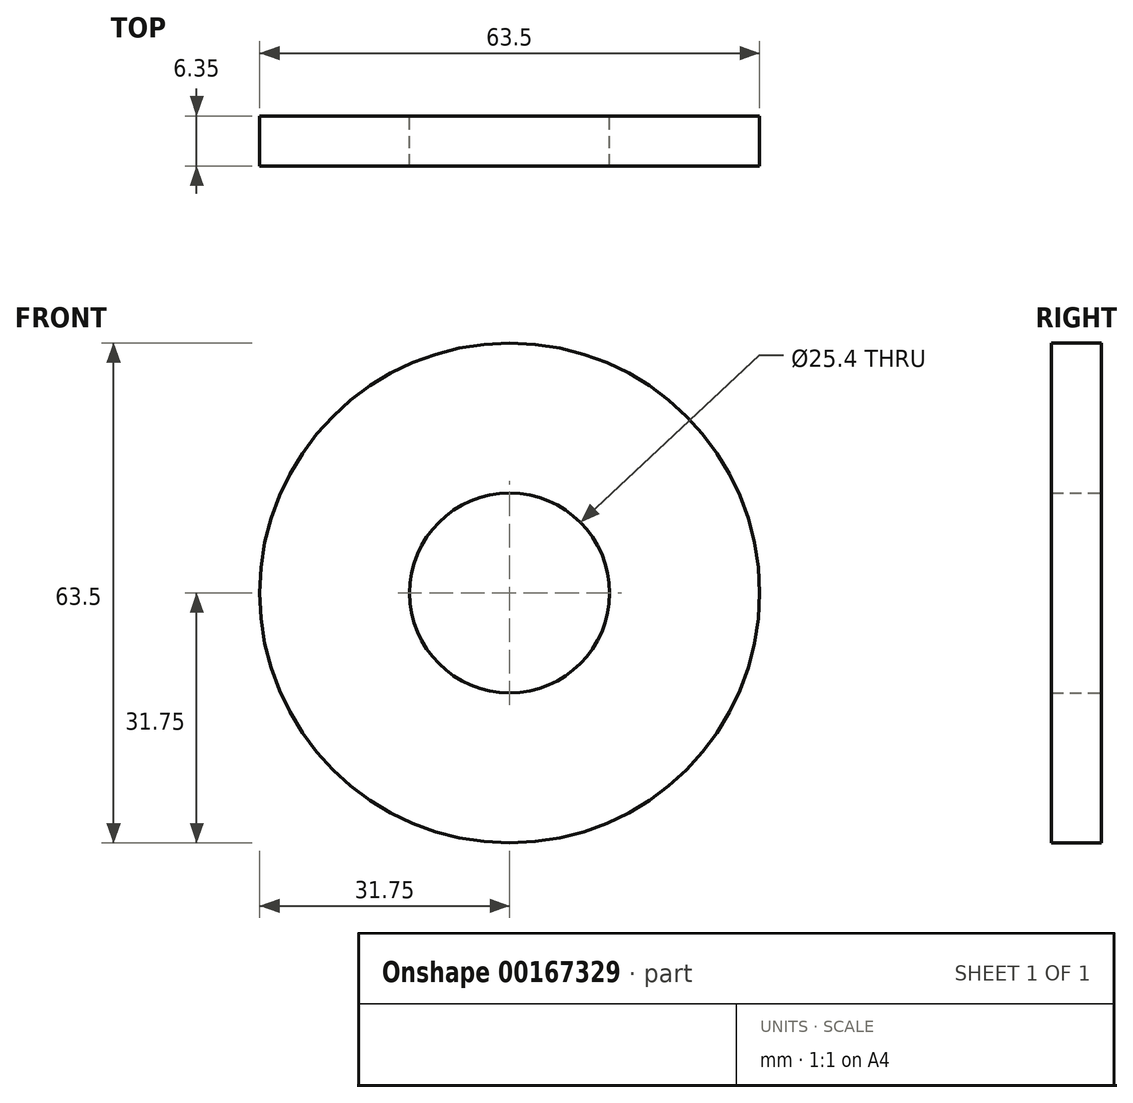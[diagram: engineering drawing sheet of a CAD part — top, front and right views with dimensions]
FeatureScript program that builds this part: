
annotation { "Feature Type Name" : "Feature", "Feature Type Description" : "" }
export const myFeature = defineFeature(function(context is Context, id is Id, definition is map)
    precondition{}
    {
        {
            var Q0;
            Q0=qCreatedBy(makeId("Front.planeOp"),FACE);
            var sketch = newSketch(context, id + "F0", { "sketchPlane" : qUnion([Q0])});
            skCircle(sketch, "E0", {"center": v(0, 0) * mm, "radius": 31.75 * mm});
            skCircle(sketch, "E1", {"center": v(0, 0) * mm, "radius": 12.7 * mm});
            skLineSegment(sketch, "E2", {"start": v(-12.7, 0) * mm, "end": v(12.7, 0) * mm});
            skLineSegment(sketch, "E3", {"start": v(-31.75, 0) * mm, "end": v(31.75, 0) * mm});
            skSolve(sketch);
        }
        {
            var Q0;
            Q0 = qSketchRegion(id + "F0", true);
            extrude(context, id + "F1", {"entities" : qUnion([Q0]), "depth" : 6.35 * mm});
        }
    });
